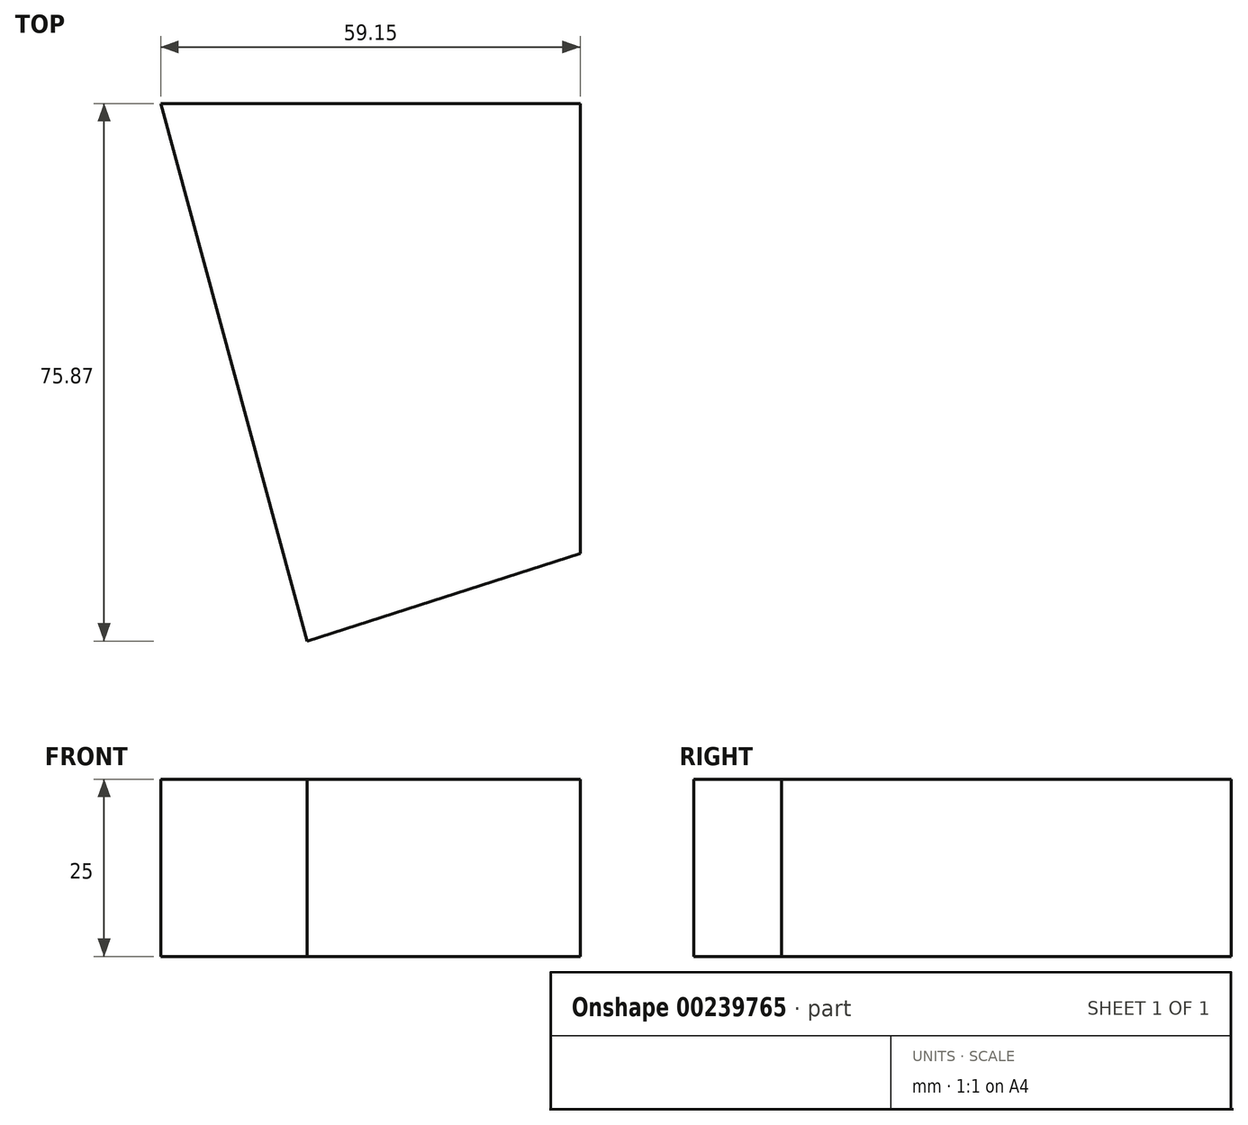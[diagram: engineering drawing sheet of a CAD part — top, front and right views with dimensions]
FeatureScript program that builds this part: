
annotation { "Feature Type Name" : "Feature", "Feature Type Description" : "" }
export const myFeature = defineFeature(function(context is Context, id is Id, definition is map)
    precondition{}
    {
        {
            var Q0;
            Q0=qCreatedBy(makeId("Top.planeOp"),FACE);
            var sketch = newSketch(context, id + "F0", { "sketchPlane" : qUnion([Q0])});
            skLineSegment(sketch, "E0", {"start": v(-38.94, 35.03) * mm, "end": v(20.2, 35.03) * mm});
            skLineSegment(sketch, "E1", {"start": v(20.2, 35.03) * mm, "end": v(20.2, -28.46) * mm});
            skLineSegment(sketch, "E2", {"start": v(20.2, -28.46) * mm, "end": v(-18.28, -40.84) * mm});
            skLineSegment(sketch, "E3", {"start": v(-18.28, -40.84) * mm, "end": v(-38.94, 35.03) * mm});
            skSolve(sketch);
        }
        {
            var Q0;
            Q0 = qSketchRegion(id + "F0", true);
            extrude(context, id + "F1", {"entities" : qUnion([Q0]), "depth" : 25 * mm});
        }
        {
            var Q0;
            Q0=qCreatedBy(makeId("Front.planeOp"),FACE);
            var sketch = newSketch(context, id + "F2", { "sketchPlane" : qUnion([Q0])});
            skFitSpline(sketch, "E4", {"points": [v(-63.69, -16.25) * mm, v(-62.23, 10.9) * mm, v(-42.82, 9.76) * mm, v(-22.97, 23.2) * mm, v(37.93, 26.02) * mm, v(43.53, -1.32) * mm, v(-20.52, -21.54) * mm, v(-14.54, -35.93) * mm, v(-41.15, -34.61) * mm], "startDerivative": vector(-45.22, 314.47) * mm, "endDerivative": vector(-347.9, 68.8) * mm});
            skSolve(sketch);
        }
    });
